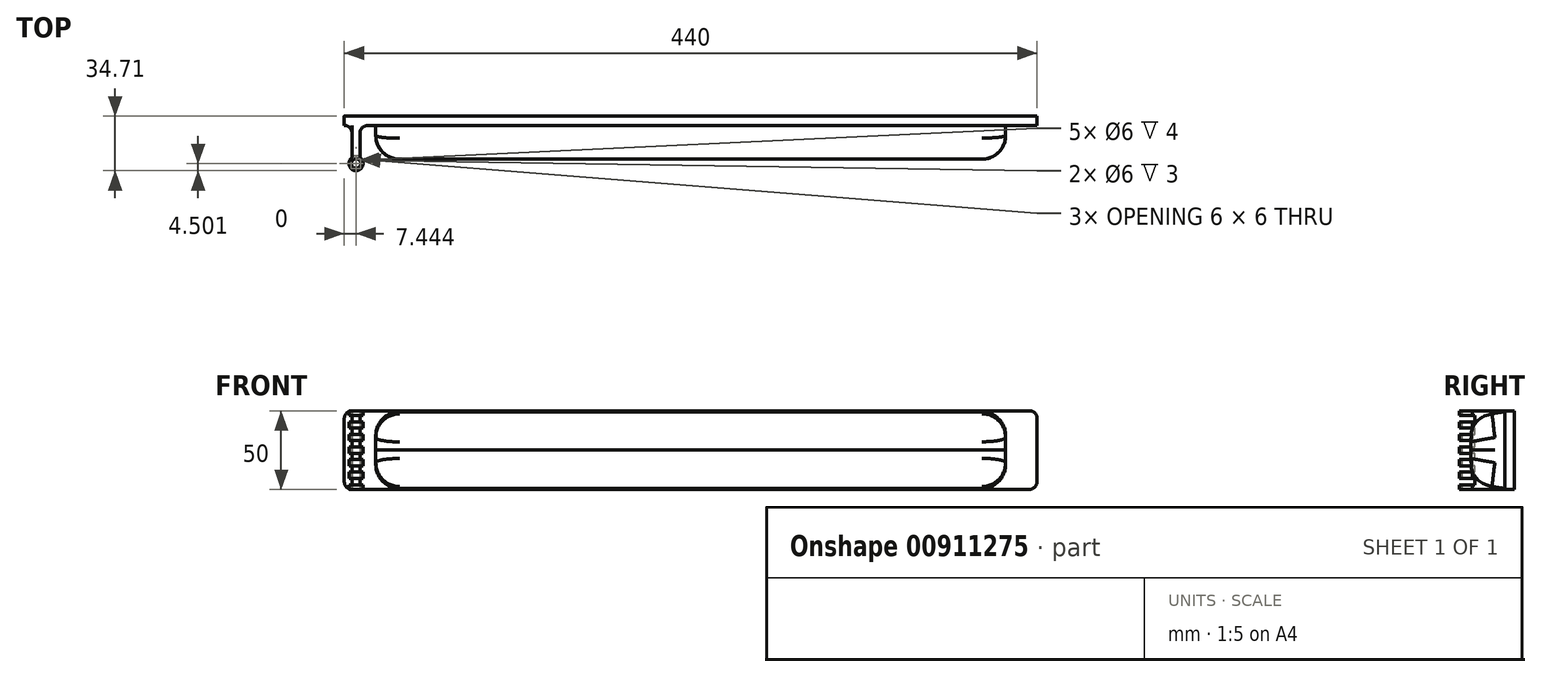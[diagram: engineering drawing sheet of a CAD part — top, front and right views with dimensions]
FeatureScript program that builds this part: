
annotation { "Feature Type Name" : "Feature", "Feature Type Description" : "" }
export const myFeature = defineFeature(function(context is Context, id is Id, definition is map)
    precondition{}
    {
        {
            var Q0;
            Q0=qCreatedBy(makeId("Front.planeOp"),FACE);
            var sketch = newSketch(context, id + "F0", { "sketchPlane" : qUnion([Q0])});
            skLineSegment(sketch, "E0", {"start": v(0, 0) * mm, "end": v(215, 0) * mm});
            skLineSegment(sketch, "E1.MirrorCS", {"start": v(0, 0) * mm, "end": v(-215, 0) * mm});
            skLineSegment(sketch, "E2", {"start": v(-220, 5) * mm, "end": v(-220, 45) * mm});
            skLineSegment(sketch, "E3.MirrorCS", {"start": v(220, 5) * mm, "end": v(220, 45) * mm});
            skLineSegment(sketch, "E4", {"start": v(-215, 50) * mm, "end": v(215, 50) * mm});
            skPoint(sketch, "E5.visualSharp", {"position": v(-220, 50) * mm});
            skArc(sketch, "E5.filletArc", {"start": v(-215, 50) * mm, "mid": v(-218.54, 48.54) * mm, "end": v(-220, 45) * mm});
            skPoint(sketch, "E6.visualSharp", {"position": v(-220, 0) * mm});
            skArc(sketch, "E6.filletArc", {"start": v(-220, 5) * mm, "mid": v(-218.54, 1.46) * mm, "end": v(-215, 0) * mm});
            skPoint(sketch, "E7.visualSharp", {"position": v(220, 50) * mm});
            skArc(sketch, "E7.filletArc", {"start": v(220, 45) * mm, "mid": v(218.54, 48.54) * mm, "end": v(215, 50) * mm});
            skPoint(sketch, "E8.visualSharp", {"position": v(220, 0) * mm});
            skArc(sketch, "E8.filletArc", {"start": v(215, 0) * mm, "mid": v(218.54, 1.46) * mm, "end": v(220, 5) * mm});
            skPoint(sketch, "E9.start.orphan", {"position": v(0, 76.62) * mm});
            skSolve(sketch);
        }
        {
            var Q0;
            Q0=makeQuery(id+"F0.imprint","IMPRINT",FACE,{"disambiguationData":[TD([[makeQuery(id+"F0.imprint","IMPRINT",EDGE,{"derivedFrom":sQuery(id+"F0.wireOp",EDGE,"E0")}),1.0]])]});
            extrude(context, id + "F1", {"entities" : qUnion([Q0]), "depth" : 6 * mm, "offsetDistance" : 25 * mm});
        }
        {
            var Q0;
            Q0=qCreatedBy(makeId("Right.planeOp"),FACE);
            var sketch = newSketch(context, id + "F2", { "sketchPlane" : qUnion([Q0])});
            skLineSegment(sketch, "E10", {"start": v(0, 0) * mm, "end": v(0, 25) * mm});
            skLineSegment(sketch, "E11", {"start": v(0, 25) * mm, "end": v(-6.05, 25) * mm});
            skFitSpline(sketch, "E12", {"points": [v(-27.4, 25) * mm, v(-26.12, 39.67) * mm, v(-20.72, 45.62) * mm, v(-6.05, 49.35) * mm], "startDerivative": vector(0.8, 82.21) * mm, "endDerivative": vector(47.14, 6.19) * mm});
            skFitSpline(sketch, "E13.MirrorCS", {"points": [v(-27.4, 25) * mm, v(-26.12, 10.33) * mm, v(-20.72, 4.38) * mm, v(-6.05, 0.65) * mm], "startDerivative": vector(0.8, -82.21) * mm, "endDerivative": vector(47.14, -6.19) * mm});
            skLineSegment(sketch, "E14", {"start": v(-6.05, 49.35) * mm, "end": v(-6.05, 0.65) * mm});
            skSolve(sketch);
        }
        {
            var Q0;
            Q0=qSketchRegion(id+"F2",true);
            extrude(context, id + "F3", {"entities" : qUnion([Q0]), "endBound" : BoundingType.SYMMETRIC, "depth" : 400 * mm, "offsetDistance" : 25 * mm});
        }
        {
            var Q0;
            Q0=qCreatedBy(makeId("Top.planeOp"),FACE);
            cPlane(context, id + "F4", {"entities" : qUnion([Q0]), "cplaneType" : CPlaneType.OFFSET, "offset" : 25 * mm, "width" : 150 * mm, "height" : 150 * mm});
        }
        {
            var Q0;
            Q0=makeQuery(id+"F3.opExtrude","CAP_EDGE",EDGE,{"disambiguationData":[OSD([sQuery(id+"F2.wireOp",EDGE,"E13.MirrorCS")])],"isStart":true});
            var Q1;
            Q1=makeQuery(id+"F3.opExtrude","CAP_EDGE",EDGE,{"disambiguationData":[OSD([sQuery(id+"F2.wireOp",EDGE,"E12")])],"isStart":true});
            var Q2;
            Q2=makeQuery(id+"F3.opExtrude","CAP_EDGE",EDGE,{"disambiguationData":[OSD([sQuery(id+"F2.wireOp",EDGE,"E13.MirrorCS")])],"isStart":false});
            var Q3;
            Q3=makeQuery(id+"F3.opExtrude","CAP_EDGE",EDGE,{"disambiguationData":[OSD([sQuery(id+"F2.wireOp",EDGE,"E12")])],"isStart":false});
            fillet(context, id + "F5", {"entities" : qUnion([Q0, Q1, Q2, Q3]), "radius" : 15 * mm, "tangentPropagation" : true, "allowEdgeOverflow" : false});
        }
        {
            var Q0;
            Q0=qCreatedBy(id+"F4.planeOp",FACE);
            var sketch = newSketch(context, id + "F6", { "sketchPlane" : qUnion([Q0])});
            skLineSegment(sketch, "E15", {"start": v(-212.56, -30.2) * mm, "end": v(-164.46, -30.2) * mm});
            skLineSegment(sketch, "E16", {"start": v(-164.46, -30.2) * mm, "end": v(-164.46, -25.2) * mm});
            skCircle(sketch, "E17", {"center": v(-212.56, -30.2) * mm, "radius": 3 * mm});
            skArc(sketch, "E18", {"start": v(-215.06, -26.47) * mm, "mid": v(-212.56, -34.7) * mm, "end": v(-210.06, -26.47) * mm});
            skLineSegment(sketch, "E19", {"start": v(-215.06, -26.47) * mm, "end": v(-215.06, 0) * mm});
            skLineSegment(sketch, "E20.MirrorCS", {"start": v(-210.06, -26.47) * mm, "end": v(-210.06, 0) * mm});
            skLineSegment(sketch, "E21", {"start": v(-215.06, 0) * mm, "end": v(-210.06, 0) * mm});
            skPoint(sketch, "E22.start.orphan", {"position": v(-212.56, 0) * mm});
            skSolve(sketch);
        }
        {
            var Q0;
            Q0=qSketchRegion(id+"F6",true);
            extrude(context, id + "F7", {"entities" : qUnion([Q0]), "operationType" : NewBodyOperationType.ADD, "endBound" : BoundingType.SYMMETRIC, "depth" : 50 * mm, "offsetDistance" : 25 * mm});
        }
        {
            var Q0;
            Q0=makeQuery(id+"F7.boolean.opBoolean","INTERSECT",EDGE,{"derivedFrom":[makeQuery(id+"F1.opExtrude","CAP_FACE",FACE,{"disambiguationData":[OSD([sQuery(id+"F0.wireOp",EDGE,"E0"),sQuery(id+"F0.wireOp",EDGE,"E1.MirrorCS"),sQuery(id+"F0.wireOp",EDGE,"E2"),sQuery(id+"F0.wireOp",EDGE,"E3.MirrorCS"),sQuery(id+"F0.wireOp",EDGE,"E4"),sQuery(id+"F0.wireOp",EDGE,"E5.filletArc"),sQuery(id+"F0.wireOp",EDGE,"E6.filletArc"),sQuery(id+"F0.wireOp",EDGE,"E7.filletArc"),sQuery(id+"F0.wireOp",EDGE,"E8.filletArc")])],"isStart":false}),makeQuery(id+"F7.opExtrude","SWEPT_FACE",FACE,{"disambiguationData":[OSD([sQuery(id+"F6.wireOp",EDGE,"E20.MirrorCS")])]})]});
            var Q1;
            Q1=makeQuery(id+"F7.boolean.opBoolean","INTERSECT",EDGE,{"derivedFrom":[makeQuery(id+"F1.opExtrude","CAP_FACE",FACE,{"disambiguationData":[OSD([sQuery(id+"F0.wireOp",EDGE,"E0"),sQuery(id+"F0.wireOp",EDGE,"E1.MirrorCS"),sQuery(id+"F0.wireOp",EDGE,"E2"),sQuery(id+"F0.wireOp",EDGE,"E3.MirrorCS"),sQuery(id+"F0.wireOp",EDGE,"E4"),sQuery(id+"F0.wireOp",EDGE,"E5.filletArc"),sQuery(id+"F0.wireOp",EDGE,"E6.filletArc"),sQuery(id+"F0.wireOp",EDGE,"E7.filletArc"),sQuery(id+"F0.wireOp",EDGE,"E8.filletArc")])],"isStart":false}),makeQuery(id+"F7.opExtrude","SWEPT_FACE",FACE,{"disambiguationData":[OSD([sQuery(id+"F6.wireOp",EDGE,"E19")])]})]});
            fillet(context, id + "F8", {"entities" : qUnion([Q0, Q1]), "radius" : 5 * mm, "tangentPropagation" : true, "allowEdgeOverflow" : false});
        }
        {
            var Q0;
            Q0=qCreatedBy(makeId("Front.planeOp"),FACE);
            cPlane(context, id + "F9", {"entities" : qUnion([Q0]), "cplaneType" : CPlaneType.OFFSET, "offset" : 40 * mm, "width" : 150 * mm, "height" : 150 * mm});
        }
        {
            var Q0;
            Q0=qCreatedBy(id+"F9.planeOp",FACE);
            var sketch = newSketch(context, id + "F10", { "sketchPlane" : qUnion([Q0])});
            skLineSegment(sketch, "E23", {"start": v(-212.15, 25) * mm, "end": v(-212.15, 55) * mm});
            skLineSegment(sketch, "E24", {"start": v(-212.15, 27) * mm, "end": v(-217.2, 27) * mm});
            skLineSegment(sketch, "E25", {"start": v(-217.2, 27) * mm, "end": v(-217.2, 25) * mm});
            skLineSegment(sketch, "E26", {"start": v(-217.2, 27) * mm, "end": v(-217.2, 50.08) * mm});
            skLineSegment(sketch, "E27", {"start": v(-217.2, 31) * mm, "end": v(-212.15, 31) * mm});
            skLineSegment(sketch, "E28", {"start": v(-217.2, 35) * mm, "end": v(-212.15, 35) * mm});
            skLineSegment(sketch, "E29", {"start": v(-217.2, 39) * mm, "end": v(-212.15, 39) * mm});
            skLineSegment(sketch, "E30", {"start": v(-217.2, 43) * mm, "end": v(-212.15, 43) * mm});
            skLineSegment(sketch, "E31", {"start": v(-217.2, 47) * mm, "end": v(-212.15, 47) * mm});
            skLineSegment(sketch, "E32", {"start": v(-217.2, 51) * mm, "end": v(-212.15, 51) * mm});
            skLineSegment(sketch, "E33", {"start": v(-217.2, 51) * mm, "end": v(-217.2, 50.08) * mm});
            skLineSegment(sketch, "E34.MirrorCS", {"start": v(-207.1, 27) * mm, "end": v(-207.1, 50.08) * mm});
            skLineSegment(sketch, "E35.MirrorCS", {"start": v(-207.1, 51) * mm, "end": v(-207.1, 50.08) * mm});
            skLineSegment(sketch, "E36.MirrorCS", {"start": v(-207.1, 51) * mm, "end": v(-212.15, 51) * mm});
            skLineSegment(sketch, "E37.MirrorCS", {"start": v(-207.1, 47) * mm, "end": v(-212.15, 47) * mm});
            skLineSegment(sketch, "E38.MirrorCS", {"start": v(-207.1, 43) * mm, "end": v(-212.15, 43) * mm});
            skLineSegment(sketch, "E39.MirrorCS", {"start": v(-207.1, 39) * mm, "end": v(-212.15, 39) * mm});
            skLineSegment(sketch, "E40.MirrorCS", {"start": v(-207.1, 35) * mm, "end": v(-212.15, 35) * mm});
            skLineSegment(sketch, "E41.MirrorCS", {"start": v(-207.1, 31) * mm, "end": v(-212.15, 31) * mm});
            skLineSegment(sketch, "E42.MirrorCS", {"start": v(-212.15, 27) * mm, "end": v(-207.1, 27) * mm});
            skLineSegment(sketch, "E43.MirrorCS", {"start": v(-207.1, 27) * mm, "end": v(-207.1, 25) * mm});
            skLineSegment(sketch, "E44.MirrorCS", {"start": v(-212.15, 25) * mm, "end": v(-212.15, -5) * mm});
            skLineSegment(sketch, "E45.MirrorCS", {"start": v(-207.1, 23) * mm, "end": v(-207.1, -0.08) * mm});
            skLineSegment(sketch, "E46.MirrorCS", {"start": v(-217.2, 23) * mm, "end": v(-217.2, -0.08) * mm});
            skLineSegment(sketch, "E47.MirrorCS", {"start": v(-217.2, 23) * mm, "end": v(-217.2, 25) * mm});
            skLineSegment(sketch, "E48.MirrorCS", {"start": v(-207.1, 23) * mm, "end": v(-207.1, 25) * mm});
            skLineSegment(sketch, "E49.MirrorCS", {"start": v(-212.15, 23) * mm, "end": v(-207.1, 23) * mm});
            skLineSegment(sketch, "E50.MirrorCS", {"start": v(-212.15, 23) * mm, "end": v(-217.2, 23) * mm});
            skLineSegment(sketch, "E51.MirrorCS", {"start": v(-217.2, 19) * mm, "end": v(-212.15, 19) * mm});
            skLineSegment(sketch, "E52.MirrorCS", {"start": v(-217.2, 15) * mm, "end": v(-212.15, 15) * mm});
            skLineSegment(sketch, "E53.MirrorCS", {"start": v(-207.1, 15) * mm, "end": v(-212.15, 15) * mm});
            skLineSegment(sketch, "E54.MirrorCS", {"start": v(-207.1, 19) * mm, "end": v(-212.15, 19) * mm});
            skLineSegment(sketch, "E55.MirrorCS", {"start": v(-207.1, 11) * mm, "end": v(-212.15, 11) * mm});
            skLineSegment(sketch, "E56.MirrorCS", {"start": v(-217.2, 11) * mm, "end": v(-212.15, 11) * mm});
            skLineSegment(sketch, "E57.MirrorCS", {"start": v(-217.2, 7) * mm, "end": v(-212.15, 7) * mm});
            skLineSegment(sketch, "E58.MirrorCS", {"start": v(-207.1, 7) * mm, "end": v(-212.15, 7) * mm});
            skLineSegment(sketch, "E59.MirrorCS", {"start": v(-207.1, 3) * mm, "end": v(-212.15, 3) * mm});
            skLineSegment(sketch, "E60.MirrorCS", {"start": v(-217.2, 3) * mm, "end": v(-212.15, 3) * mm});
            skLineSegment(sketch, "E61.MirrorCS", {"start": v(-217.2, -1) * mm, "end": v(-217.2, -0.08) * mm});
            skLineSegment(sketch, "E62.MirrorCS", {"start": v(-217.2, -1) * mm, "end": v(-212.15, -1) * mm});
            skLineSegment(sketch, "E63.MirrorCS", {"start": v(-207.1, -1) * mm, "end": v(-207.1, -0.08) * mm});
            skLineSegment(sketch, "E64.MirrorCS", {"start": v(-207.1, -1) * mm, "end": v(-212.15, -1) * mm});
            skSolve(sketch);
        }
        {
            var Q0;
            {var subQ0=sQuery(id+"F10.wireOp",EDGE,"E30");Q0=makeQuery(id+"F10.imprint","IMPRINT",FACE,{"disambiguationData":[TD([[makeQuery(id+"F10.imprint","IMPRINT",EDGE,{"derivedFrom":subQ0}),1.0]])]});}
            var Q1;
            {var subQ2=sQuery(id+"F10.wireOp",EDGE,"E37.MirrorCS");Q1=makeQuery(id+"F10.imprint","IMPRINT",FACE,{"disambiguationData":[TD([[makeQuery(id+"F10.imprint","IMPRINT",EDGE,{"derivedFrom":subQ2}),1.0]])]});}
            var Q2;
            {var subQ2=sQuery(id+"F10.wireOp",EDGE,"E39.MirrorCS");Q2=makeQuery(id+"F10.imprint","IMPRINT",FACE,{"disambiguationData":[TD([[makeQuery(id+"F10.imprint","IMPRINT",EDGE,{"derivedFrom":subQ2}),1.0]])]});}
            var Q3;
            {var subQ0=sQuery(id+"F10.wireOp",EDGE,"E24");Q3=makeQuery(id+"F10.imprint","IMPRINT",FACE,{"disambiguationData":[TD([[makeQuery(id+"F10.imprint","IMPRINT",EDGE,{"derivedFrom":subQ0}),-1.0]])]});}
            var Q4;
            {var subQ2=sQuery(id+"F10.wireOp",EDGE,"E41.MirrorCS");Q4=makeQuery(id+"F10.imprint","IMPRINT",FACE,{"disambiguationData":[TD([[makeQuery(id+"F10.imprint","IMPRINT",EDGE,{"derivedFrom":subQ2}),1.0]])]});}
            var Q5;
            {var subQ0=sQuery(id+"F10.wireOp",EDGE,"E49.MirrorCS");Q5=makeQuery(id+"F10.imprint","IMPRINT",FACE,{"disambiguationData":[TD([[makeQuery(id+"F10.imprint","IMPRINT",EDGE,{"derivedFrom":subQ0}),-1.0]])]});}
            var Q6;
            {var subQ0=sQuery(id+"F10.wireOp",EDGE,"E50.MirrorCS");Q6=makeQuery(id+"F10.imprint","IMPRINT",FACE,{"disambiguationData":[TD([[makeQuery(id+"F10.imprint","IMPRINT",EDGE,{"derivedFrom":subQ0}),1.0]])]});}
            var Q7;
            {var subQ0=sQuery(id+"F10.wireOp",EDGE,"E52.MirrorCS");Q7=makeQuery(id+"F10.imprint","IMPRINT",FACE,{"disambiguationData":[TD([[makeQuery(id+"F10.imprint","IMPRINT",EDGE,{"derivedFrom":subQ0}),-1.0]])]});}
            var Q8;
            {var subQ0=sQuery(id+"F10.wireOp",EDGE,"E53.MirrorCS");Q8=makeQuery(id+"F10.imprint","IMPRINT",FACE,{"disambiguationData":[TD([[makeQuery(id+"F10.imprint","IMPRINT",EDGE,{"derivedFrom":subQ0}),1.0]])]});}
            var Q9;
            {var subQ0=sQuery(id+"F10.wireOp",EDGE,"E57.MirrorCS");Q9=makeQuery(id+"F10.imprint","IMPRINT",FACE,{"disambiguationData":[TD([[makeQuery(id+"F10.imprint","IMPRINT",EDGE,{"derivedFrom":subQ0}),-1.0]])]});}
            var Q10;
            {var subQ0=sQuery(id+"F10.wireOp",EDGE,"E58.MirrorCS");Q10=makeQuery(id+"F10.imprint","IMPRINT",FACE,{"disambiguationData":[TD([[makeQuery(id+"F10.imprint","IMPRINT",EDGE,{"derivedFrom":subQ0}),1.0]])]});}
            var Q11;
            {var subQ0=sQuery(id+"F10.wireOp",EDGE,"E28");Q11=makeQuery(id+"F10.imprint","IMPRINT",FACE,{"disambiguationData":[TD([[makeQuery(id+"F10.imprint","IMPRINT",EDGE,{"derivedFrom":subQ0}),1.0]])]});}
            extrude(context, id + "F11", {"entities" : qUnion([Q0, Q1, Q2, Q3, Q4, Q5, Q6, Q7, Q8, Q9, Q10, Q11]), "operationType" : NewBodyOperationType.REMOVE, "oppositeDirection" : true, "depth" : 15 * mm, "offsetDistance" : 25 * mm});
        }
    });
